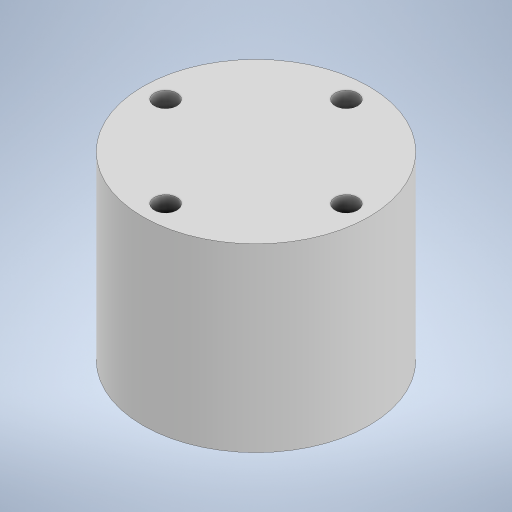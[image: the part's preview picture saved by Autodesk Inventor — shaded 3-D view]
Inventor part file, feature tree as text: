
AUTODESK INVENTOR PART (.ipt)
format: ipt  version: 2024 (Build 280153000, 153)  size: 202,752 bytes
history: native  units: in
note: dims shown in document units (in); Inventor stores cm internally (conversion verified against a paired STEP export)
features: extrude x2, sketch x2
ambient origin geometry x8: Origin, YZ Plane, XZ Plane, XY Plane, X Axis, Y Axis, Z Axis, Center Point
bodies: Solid1 (feature_tree)
feature tree (4):
  extrude  "Extrusion1"  Depth=2.0in TaperAngle=0.0deg
  extrude  "Extrusion2"  TaperAngle=0.0deg  [1 undecoded]
  sketch  "Sketch1"  dims[d0=2.5in d1=2.0in d2=0.0in]
  sketch  "Sketch2"  dims[d3=0.25in d6=0.0in d7=1.0in d8=1.5748in d10=360.0deg d12=2.0in d13=0.0in]
note: 1 required parameter value undecoded (feature->parameter linkage not recoverable at this tier; creation-order binding heuristic only, values carry confidence <= 0.55)
